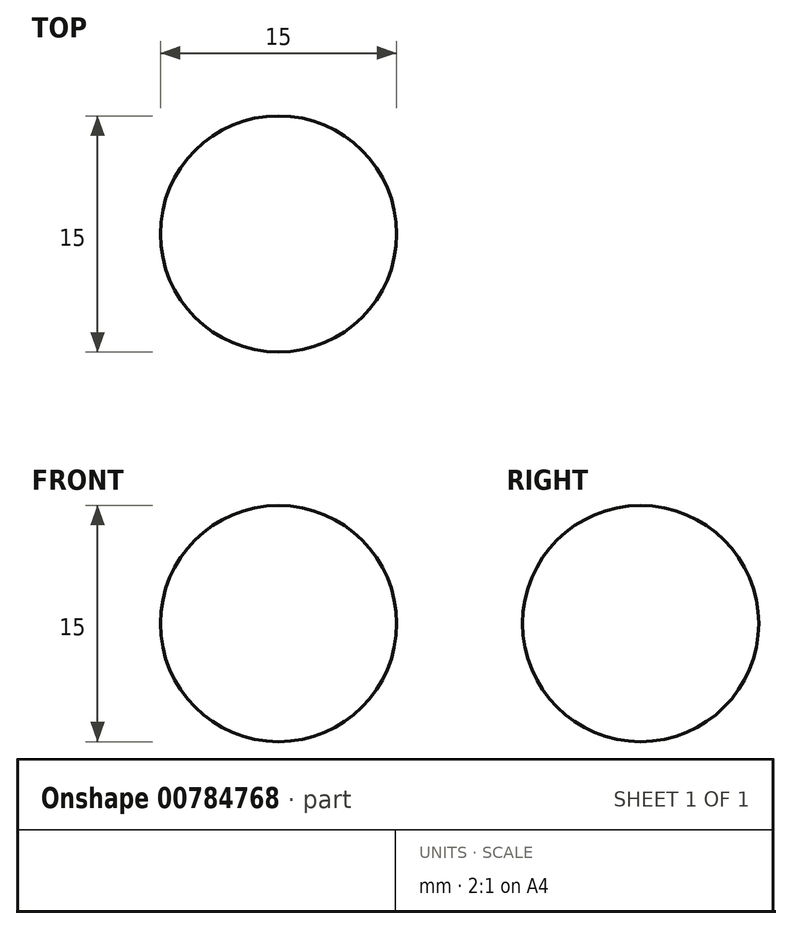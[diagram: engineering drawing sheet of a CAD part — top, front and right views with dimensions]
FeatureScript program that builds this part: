
annotation { "Feature Type Name" : "Feature", "Feature Type Description" : "" }
export const myFeature = defineFeature(function(context is Context, id is Id, definition is map)
    precondition{}
    {
        {
            var Q0;
            Q0=qCreatedBy(makeId("Top.planeOp"),FACE);
            var sketch = newSketch(context, id + "F0", { "sketchPlane" : qUnion([Q0])});
            skArc(sketch, "E0", {"start": v(0, 7.5) * mm, "mid": v(-7.5, 0) * mm, "end": v(0, -7.5) * mm});
            skLineSegment(sketch, "E1", {"start": v(0, 7.5) * mm, "end": v(0, -7.5) * mm});
            skSolve(sketch);
        }
        {
            var Q0;
            Q0=qSketchRegion(id+"F0",true);
            var Q1;
            Q1=sQuery(id+"F0.wireOp",EDGE,"E1");
            revolve(context, id + "F1", {"surfaceOperationType" : NewSurfaceOperationType.NEW, "entities" : qUnion([Q0]), "axis" : qUnion([Q1]), "revolveType" : RevolveType.FULL});
        }
    });
